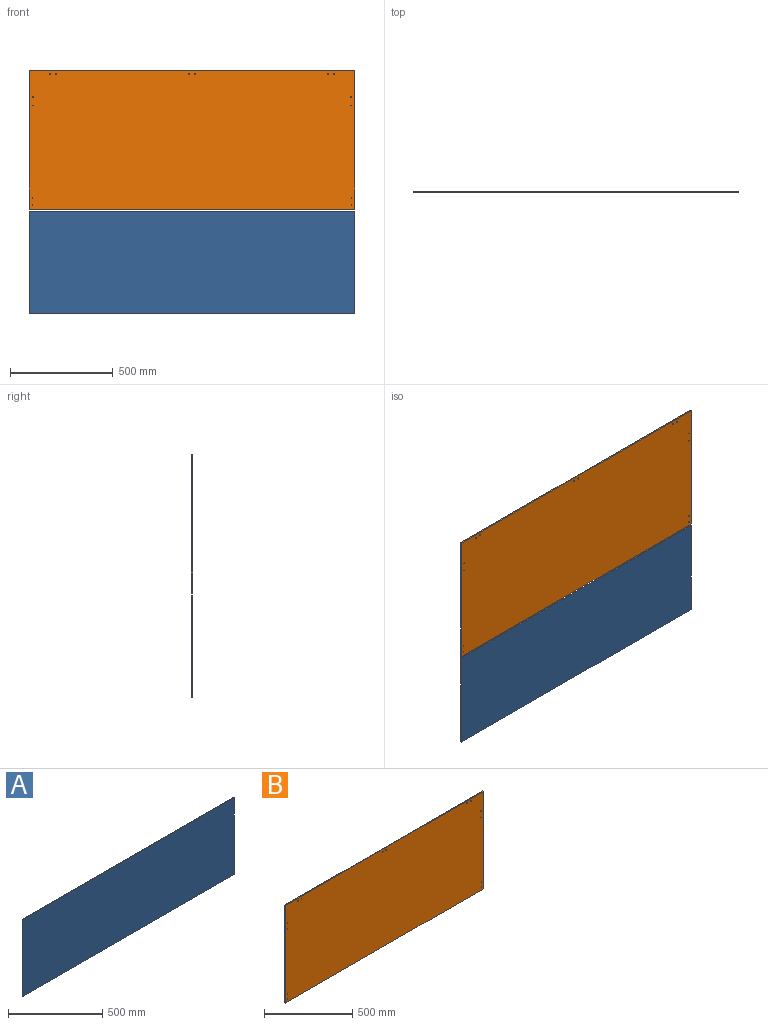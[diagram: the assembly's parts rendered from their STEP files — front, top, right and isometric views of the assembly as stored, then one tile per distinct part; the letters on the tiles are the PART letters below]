
ASSEMBLY  parts=2 mates=1
PART A: 6 faces, bbox 1585x6x500 mm
  f0: plane 500x6mm, normal (-1,0,0), area 3000mm2, adj f1,f3,f4,f5
  f1: plane 1585x6mm, normal (0,0,-1), area 9510mm2, adj f0,f2,f4,f5
  f2: plane 500x6mm, normal (1,0,0), area 3000mm2, adj f1,f3,f4,f5
  f3: plane 1585x6mm, normal (0,0,1), area 9510mm2, adj f0,f2,f4,f5
  f4: plane 1585x500mm, normal (0,1,0), area 792500mm2, adj f0,f1,f2,f3
  f5: plane 1585x500mm, normal (0,-1,0), area 792500mm2, adj f0,f1,f2,f3
PART B: 20 faces, bbox 1585x6x677 mm
  f0: plane 1585x6mm, normal (0,0,1), area 9510mm2, adj f1,f17,f18,f19
  f1: plane 677x6mm, normal (-1,0,0), area 4062mm2, adj f0,f2,f18,f19
  f2: plane 1585x6mm, normal (0,0,-1), area 9510mm2, adj f1,f17,f18,f19
  f3: cylinder r=3.4mm len=6.8mm, axis (0,-1,0), area 128.2mm2, adj f18,f19
  f4: cylinder r=3.4mm len=6.8mm, axis (0,-1,0), area 128.2mm2, adj f18,f19
  f5: cylinder r=3.4mm len=6.8mm, axis (0,-1,0), area 128.2mm2, adj f18,f19
  f6: cylinder r=3.4mm len=6.8mm, axis (0,-1,0), area 128.2mm2, adj f18,f19
  f7: cylinder r=3.4mm len=6.8mm, axis (0,-1,0), area 128.2mm2, adj f18,f19
  f8: cylinder r=3.4mm len=6.8mm, axis (0,-1,0), area 128.2mm2, adj f18,f19
  f9: cylinder r=2mm len=6mm, axis (0,-1,0), area 75.4mm2, adj f18,f19
  f10: cylinder r=2mm len=6mm, axis (0,-1,0), area 75.4mm2, adj f18,f19
  f11: cylinder r=2mm len=6mm, axis (0,-1,0), area 75.4mm2, adj f18,f19
  f12: cylinder r=2mm len=6mm, axis (0,-1,0), area 75.4mm2, adj f18,f19
  f13: cylinder r=2mm len=6mm, axis (0,-1,0), area 75.4mm2, adj f18,f19
  f14: cylinder r=2mm len=6mm, axis (0,-1,0), area 75.4mm2, adj f18,f19
  f15: cylinder r=2mm len=6mm, axis (0,-1,0), area 75.4mm2, adj f18,f19
  f16: cylinder r=2mm len=6mm, axis (0,-1,0), area 75.4mm2, adj f18,f19
  f17: plane 677x6mm, normal (1,0,0), area 4062mm2, adj f0,f2,f18,f19
  f18: plane 1585x677mm, normal (0,1,0), area 1072726.6mm2, adj f0,f1,f2,f3,f4,f5,f6,f7
  f19: plane 1585x677mm, normal (0,-1,0), area 1072726.6mm2, adj f0,f1,f2,f3,f4,f5,f6,f7
PLACE A t=(0,0,-1197.5)mm
PLACE B t=(0,0,-10.5)mm
MATE parallel A.f3 <-> B.f2  axis (0,0,1) through (792.5,3,-697.5)mm
